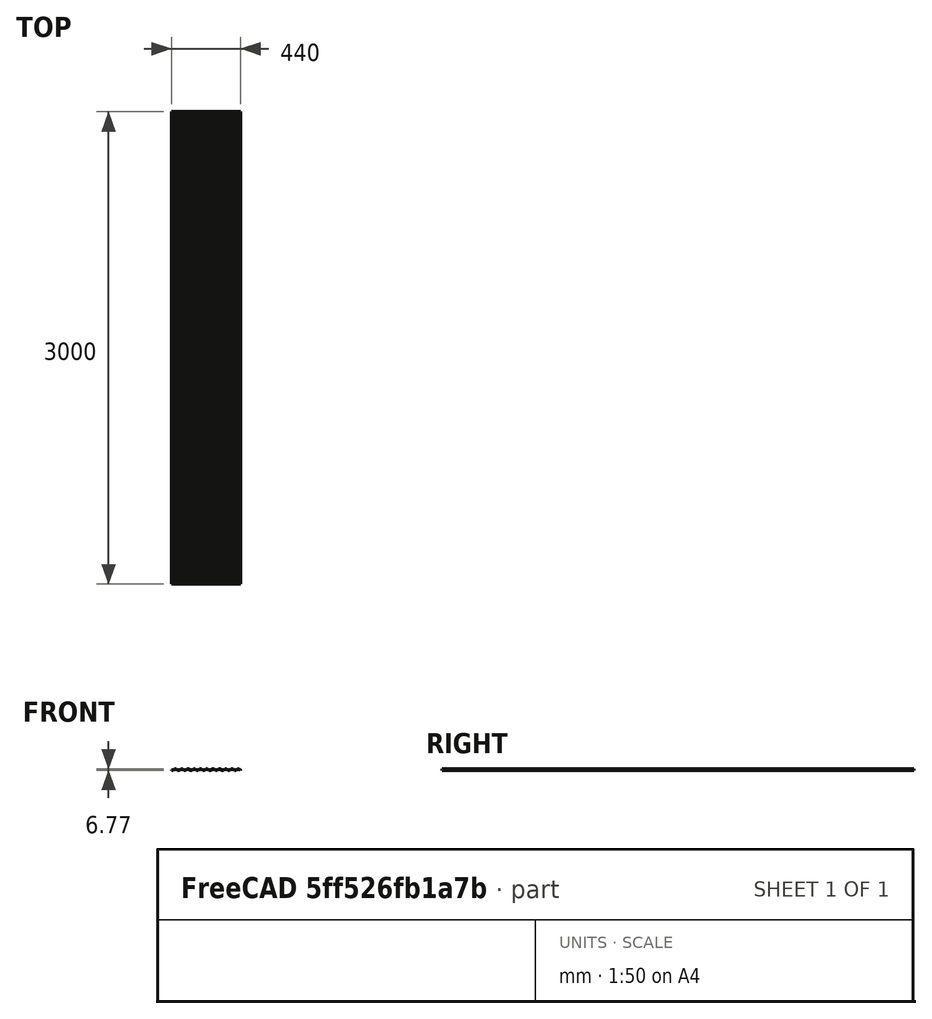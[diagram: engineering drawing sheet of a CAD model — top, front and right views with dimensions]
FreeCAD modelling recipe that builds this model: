
FCSTD DOCUMENT  (FreeCAD 1.0R38641 +468 (Git))
Label: vlnity-plech
License: All rights reserved
LicenseURL: https://en.wikipedia.org/wiki/All_rights_reserved
objects: Sketcher::SketchObject×1, PartDesign::Pad×1, PartDesign::Body×1
note: 6 computed .brp shape members not serialized (recipe doc carries the construction recipe); baked Part::Feature solids carry a one-line shape summary decoded from their .brp

FEATURE [Sketcher::SketchObject] Sketch
  ArcFitTolerance = 1e-06
  AttachmentSupport = -> [XZ_Plane]
  FullyConstrained = true
  MakeInternals = false
  MapMode = 5
  Placement = pos=(0,0,0) rot=(1,0,0;1.5708rad)
  sketch-geometry (90):
    g0: LineSegment StartX=0 StartY=0 StartZ=0 EndX=10 EndY=0 EndZ=0
    g1: LineSegment StartX=10 StartY=0 StartZ=0 EndX=20 EndY=5.7735 EndZ=0
    g2: LineSegment StartX=20 StartY=5.7735 StartZ=0 EndX=30 EndY=5.7735 EndZ=0
    g3: LineSegment StartX=30 StartY=5.7735 StartZ=0 EndX=40 EndY=0 EndZ=0
    g4: LineSegment StartX=0 StartY=1 StartZ=0 EndX=10 EndY=1 EndZ=0
    g5: LineSegment StartX=10 StartY=1 StartZ=0 EndX=20 EndY=6.7735 EndZ=0
    g6: LineSegment StartX=20 StartY=6.7735 StartZ=0 EndX=30 EndY=6.7735 EndZ=0
    g7: LineSegment StartX=30 StartY=6.7735 StartZ=0 EndX=40 EndY=1 EndZ=0
    g8: LineSegment StartX=40 StartY=0 StartZ=0 EndX=50 EndY=0 EndZ=0
    g9: LineSegment StartX=50 StartY=0 StartZ=0 EndX=60 EndY=5.7735 EndZ=0
    g10: LineSegment StartX=60 StartY=5.7735 StartZ=0 EndX=70 EndY=5.7735 EndZ=0
    g11: LineSegment StartX=70 StartY=5.7735 StartZ=0 EndX=80 EndY=0 EndZ=0
    g12: LineSegment StartX=40 StartY=1 StartZ=0 EndX=50 EndY=1 EndZ=0
    g13: LineSegment StartX=50 StartY=1 StartZ=0 EndX=60 EndY=6.7735 EndZ=0
    g14: LineSegment StartX=60 StartY=6.7735 StartZ=0 EndX=70 EndY=6.7735 EndZ=0
    g15: LineSegment StartX=70 StartY=6.7735 StartZ=0 EndX=80 EndY=1 EndZ=0
    g16: LineSegment StartX=80 StartY=0 StartZ=0 EndX=90 EndY=0 EndZ=0
    g17: LineSegment StartX=90 StartY=0 StartZ=0 EndX=100 EndY=5.7735 EndZ=0
    g18: LineSegment StartX=100 StartY=5.7735 StartZ=0 EndX=110 EndY=5.7735 EndZ=0
    g19: LineSegment StartX=110 StartY=5.7735 StartZ=0 EndX=120 EndY=0 EndZ=0
    g20: LineSegment StartX=80 StartY=1 StartZ=0 EndX=90 EndY=1 EndZ=0
    g21: LineSegment StartX=90 StartY=1 StartZ=0 EndX=100 EndY=6.7735 EndZ=0
    g22: LineSegment StartX=100 StartY=6.7735 StartZ=0 EndX=110 EndY=6.7735 EndZ=0
    g23: LineSegment StartX=110 StartY=6.7735 StartZ=0 EndX=120 EndY=1 EndZ=0
    g24: LineSegment StartX=120 StartY=0 StartZ=0 EndX=130 EndY=0 EndZ=0
    g25: LineSegment StartX=130 StartY=0 StartZ=0 EndX=140 EndY=5.7735 EndZ=0
    g26: LineSegment StartX=140 StartY=5.7735 StartZ=0 EndX=150 EndY=5.7735 EndZ=0
    g27: LineSegment StartX=150 StartY=5.7735 StartZ=0 EndX=160 EndY=0 EndZ=0
    g28: LineSegment StartX=120 StartY=1 StartZ=0 EndX=130 EndY=1 EndZ=0
    g29: LineSegment StartX=130 StartY=1 StartZ=0 EndX=140 EndY=6.7735 EndZ=0
    g30: LineSegment StartX=140 StartY=6.7735 StartZ=0 EndX=150 EndY=6.7735 EndZ=0
    g31: LineSegment StartX=150 StartY=6.7735 StartZ=0 EndX=160 EndY=1 EndZ=0
    g32: LineSegment StartX=160 StartY=0 StartZ=0 EndX=170 EndY=0 EndZ=0
    g33: LineSegment StartX=170 StartY=0 StartZ=0 EndX=180 EndY=5.7735 EndZ=0
    g34: LineSegment StartX=180 StartY=5.7735 StartZ=0 EndX=190 EndY=5.7735 EndZ=0
    g35: LineSegment StartX=190 StartY=5.7735 StartZ=0 EndX=200 EndY=0 EndZ=0
    g36: LineSegment StartX=160 StartY=1 StartZ=0 EndX=170 EndY=1 EndZ=0
    g37: LineSegment StartX=170 StartY=1 StartZ=0 EndX=180 EndY=6.7735 EndZ=0
    g38: LineSegment StartX=180 StartY=6.7735 StartZ=0 EndX=190 EndY=6.7735 EndZ=0
    g39: LineSegment StartX=190 StartY=6.7735 StartZ=0 EndX=200 EndY=1 EndZ=0
    g40: LineSegment StartX=200 StartY=0 StartZ=0 EndX=210 EndY=0 EndZ=0
    g41: LineSegment StartX=210 StartY=0 StartZ=0 EndX=220 EndY=5.7735 EndZ=0
    g42: LineSegment StartX=220 StartY=5.7735 StartZ=0 EndX=230 EndY=5.7735 EndZ=0
    g43: LineSegment StartX=230 StartY=5.7735 StartZ=0 EndX=240 EndY=0 EndZ=0
    g44: LineSegment StartX=200 StartY=1 StartZ=0 EndX=210 EndY=1 EndZ=0
    g45: LineSegment StartX=210 StartY=1 StartZ=0 EndX=220 EndY=6.7735 EndZ=0
    g46: LineSegment StartX=220 StartY=6.7735 StartZ=0 EndX=230 EndY=6.7735 EndZ=0
    g47: LineSegment StartX=230 StartY=6.7735 StartZ=0 EndX=240 EndY=1 EndZ=0
    g48: LineSegment StartX=240 StartY=0 StartZ=0 EndX=250 EndY=0 EndZ=0
    g49: LineSegment StartX=250 StartY=0 StartZ=0 EndX=260 EndY=5.7735 EndZ=0
    g50: LineSegment StartX=260 StartY=5.7735 StartZ=0 EndX=270 EndY=5.7735 EndZ=0
    g51: LineSegment StartX=270 StartY=5.7735 StartZ=0 EndX=280 EndY=0 EndZ=0
    g52: LineSegment StartX=240 StartY=1 StartZ=0 EndX=250 EndY=1 EndZ=0
    g53: LineSegment StartX=250 StartY=1 StartZ=0 EndX=260 EndY=6.7735 EndZ=0
    g54: LineSegment StartX=260 StartY=6.7735 StartZ=0 EndX=270 EndY=6.7735 EndZ=0
    g55: LineSegment StartX=270 StartY=6.7735 StartZ=0 EndX=280 EndY=1 EndZ=0
    g56: LineSegment StartX=280 StartY=0 StartZ=0 EndX=290 EndY=0 EndZ=0
    g57: LineSegment StartX=290 StartY=0 StartZ=0 EndX=300 EndY=5.7735 EndZ=0
    g58: LineSegment StartX=300 StartY=5.7735 StartZ=0 EndX=310 EndY=5.7735 EndZ=0
    g59: LineSegment StartX=310 StartY=5.7735 StartZ=0 EndX=320 EndY=0 EndZ=0
    g60: LineSegment StartX=280 StartY=1 StartZ=0 EndX=290 EndY=1 EndZ=0
    g61: LineSegment StartX=290 StartY=1 StartZ=0 EndX=300 EndY=6.7735 EndZ=0
    g62: LineSegment StartX=300 StartY=6.7735 StartZ=0 EndX=310 EndY=6.7735 EndZ=0
    g63: LineSegment StartX=310 StartY=6.7735 StartZ=0 EndX=320 EndY=1 EndZ=0
    g64: LineSegment StartX=320 StartY=0 StartZ=0 EndX=330 EndY=0 EndZ=0
    g65: LineSegment StartX=330 StartY=0 StartZ=0 EndX=340 EndY=5.7735 EndZ=0
    g66: LineSegment StartX=340 StartY=5.7735 StartZ=0 EndX=350 EndY=5.7735 EndZ=0
    g67: LineSegment StartX=350 StartY=5.7735 StartZ=0 EndX=360 EndY=0 EndZ=0
    g68: LineSegment StartX=320 StartY=1 StartZ=0 EndX=330 EndY=1 EndZ=0
    g69: LineSegment StartX=330 StartY=1 StartZ=0 EndX=340 EndY=6.7735 EndZ=0
    g70: LineSegment StartX=340 StartY=6.7735 StartZ=0 EndX=350 EndY=6.7735 EndZ=0
    g71: LineSegment StartX=350 StartY=6.7735 StartZ=0 EndX=360 EndY=1 EndZ=0
    g72: LineSegment StartX=360 StartY=0 StartZ=0 EndX=370 EndY=0 EndZ=0
    g73: LineSegment StartX=370 StartY=0 StartZ=0 EndX=380 EndY=5.7735 EndZ=0
    g74: LineSegment StartX=380 StartY=5.7735 StartZ=0 EndX=390 EndY=5.7735 EndZ=0
    g75: LineSegment StartX=390 StartY=5.7735 StartZ=0 EndX=400 EndY=0 EndZ=0
    g76: LineSegment StartX=360 StartY=1 StartZ=0 EndX=370 EndY=1 EndZ=0
    g77: LineSegment StartX=370 StartY=1 StartZ=0 EndX=380 EndY=6.7735 EndZ=0
    g78: LineSegment StartX=380 StartY=6.7735 StartZ=0 EndX=390 EndY=6.7735 EndZ=0
    g79: LineSegment StartX=390 StartY=6.7735 StartZ=0 EndX=400 EndY=1 EndZ=0
    g80: LineSegment StartX=400 StartY=0 StartZ=0 EndX=410 EndY=0 EndZ=0
    g81: LineSegment StartX=410 StartY=0 StartZ=0 EndX=420 EndY=5.7735 EndZ=0
    g82: LineSegment StartX=420 StartY=5.7735 StartZ=0 EndX=430 EndY=5.7735 EndZ=0
    g83: LineSegment StartX=430 StartY=5.7735 StartZ=0 EndX=440 EndY=0 EndZ=0
    g84: LineSegment StartX=400 StartY=1 StartZ=0 EndX=410 EndY=1 EndZ=0
    g85: LineSegment StartX=410 StartY=1 StartZ=0 EndX=420 EndY=6.7735 EndZ=0
    g86: LineSegment StartX=420 StartY=6.7735 StartZ=0 EndX=430 EndY=6.7735 EndZ=0
    g87: LineSegment StartX=430 StartY=6.7735 StartZ=0 EndX=440 EndY=1 EndZ=0
    g88: LineSegment StartX=0 StartY=1 StartZ=0 EndX=0 EndY=0 EndZ=0
    g89: LineSegment StartX=440 StartY=1 StartZ=0 EndX=440 EndY=0 EndZ=0
  constraints (279):
    c: Coincident(g0,g-1)
    c: PointOnObject(g0,g-1)
    c: Coincident(g1,g0)
    c: Coincident(g2,g1)
    c: Horizontal(g2)
    c: Coincident(g3,g2)
    c: PointOnObject(g3,g-1)
    c: Equal(g0,g2)
    c: Equal(g1,g3)
    c: Angle(g-1,g1) = 0.523599
    c: DistanceX(g0,g0) = 10
    c: DistanceX(g0,g1) = 10
    c: Coincident(g5,g4)
    c: Coincident(g6,g5)
    c: Horizontal(g6)
    c: Coincident(g7,g6)
    c: Equal(g4,g6)
    c: Equal(g5,g7)
    c: DistanceX(g4,g4) = 10
    c: DistanceX(g4,g5) = 10
    c: DistanceY(g0,g4) = 1
    c: Parallel(g4,g0)
    c: Vertical(g4,g0)
    c: Parallel(g5,g1)
    c: Parallel(g7,g3)
    c: Coincident(g9,g8)
    c: Coincident(g17,g16)
    c: Coincident(g25,g24)
    c: Coincident(g33,g32)
    c: Coincident(g41,g40)
    c: Coincident(g49,g48)
    c: Coincident(g57,g56)
    c: Coincident(g65,g64)
    c: Coincident(g73,g72)
    c: Coincident(g81,g80)
    c: Coincident(g10,g9)
    c: Coincident(g18,g17)
    c: Coincident(g26,g25)
    c: Coincident(g34,g33)
    c: Coincident(g42,g41)
    c: Coincident(g50,g49)
    c: Coincident(g58,g57)
    c: Coincident(g66,g65)
    c: Coincident(g74,g73)
    c: Coincident(g82,g81)
    c: Horizontal(g10)
    c: Horizontal(g18)
    c: Horizontal(g26)
    c: Horizontal(g34)
    c: Horizontal(g42)
    c: Horizontal(g50)
    c: Horizontal(g58)
    c: Horizontal(g66)
    c: Horizontal(g74)
    c: Horizontal(g82)
    c: Coincident(g11,g10)
    c: Coincident(g19,g18)
    c: Coincident(g27,g26)
    c: Coincident(g35,g34)
    c: Coincident(g43,g42)
    c: Coincident(g51,g50)
    c: Coincident(g59,g58)
    c: Coincident(g67,g66)
    c: Coincident(g75,g74)
    c: Coincident(g83,g82)
    c: Equal(g8,g10)
    c: Equal(g16,g18)
    c: Equal(g24,g26)
    c: Equal(g32,g34)
    c: Equal(g40,g42)
    c: Equal(g48,g50)
    c: Equal(g56,g58)
    c: Equal(g64,g66)
    c: Equal(g72,g74)
    c: Equal(g80,g82)
    c: Equal(g9,g11)
    c: Equal(g17,g19)
    c: Equal(g25,g27)
    c: Equal(g33,g35)
    c: Equal(g41,g43)
    c: Equal(g49,g51)
    c: Equal(g57,g59)
    c: Equal(g65,g67)
    c: Equal(g73,g75)
    c: Equal(g81,g83)
    c: DistanceX(g8,g8) = 10
    c: DistanceX(g16,g16) = 10
    c: DistanceX(g24,g24) = 10
    c: DistanceX(g32,g32) = 10
    c: DistanceX(g40,g40) = 10
    c: DistanceX(g48,g48) = 10
    c: DistanceX(g56,g56) = 10
    c: DistanceX(g64,g64) = 10
    c: DistanceX(g72,g72) = 10
    c: DistanceX(g80,g80) = 10
    c: DistanceX(g8,g9) = 10
    c: DistanceX(g16,g17) = 10
    c: DistanceX(g24,g25) = 10
    c: DistanceX(g32,g33) = 10
    c: DistanceX(g40,g41) = 10
    c: DistanceX(g48,g49) = 10
    c: DistanceX(g56,g57) = 10
    c: DistanceX(g64,g65) = 10
    c: DistanceX(g72,g73) = 10
    c: DistanceX(g80,g81) = 10
    c: Coincident(g13,g12)
    c: Coincident(g21,g20)
    c: Coincident(g29,g28)
    c: Coincident(g37,g36)
    c: Coincident(g45,g44)
    c: Coincident(g53,g52)
    c: Coincident(g61,g60)
    c: Coincident(g69,g68)
    c: Coincident(g77,g76)
    c: Coincident(g85,g84)
    c: Coincident(g14,g13)
    c: Coincident(g22,g21)
    c: Coincident(g30,g29)
    c: Coincident(g38,g37)
    c: Coincident(g46,g45)
    c: Coincident(g54,g53)
    c: Coincident(g62,g61)
    c: Coincident(g70,g69)
    c: Coincident(g78,g77)
    c: Coincident(g86,g85)
    c: Horizontal(g14)
    c: Horizontal(g22)
    c: Horizontal(g30)
    c: Horizontal(g38)
    c: Horizontal(g46)
    c: Horizontal(g54)
    c: Horizontal(g62)
    c: Horizontal(g70)
    c: Horizontal(g78)
    c: Horizontal(g86)
    c: Coincident(g15,g14)
    c: Coincident(g23,g22)
    c: Coincident(g31,g30)
    c: Coincident(g39,g38)
    c: Coincident(g47,g46)
    c: Coincident(g55,g54)
    c: Coincident(g63,g62)
    c: Coincident(g71,g70)
    c: Coincident(g79,g78)
    c: Coincident(g87,g86)
    c: Equal(g12,g14)
    c: Equal(g20,g22)
    c: Equal(g28,g30)
    c: Equal(g36,g38)
    c: Equal(g44,g46)
    c: Equal(g52,g54)
    c: Equal(g60,g62)
    c: Equal(g68,g70)
    c: Equal(g76,g78)
    c: Equal(g84,g86)
    c: Equal(g13,g15)
    c: Equal(g21,g23)
    c: Equal(g29,g31)
    c: Equal(g37,g39)
    c: Equal(g45,g47)
    c: Equal(g53,g55)
    c: Equal(g61,g63)
    c: Equal(g69,g71)
    c: Equal(g77,g79)
    c: Equal(g85,g87)
    c: DistanceX(g12,g12) = 10
    c: DistanceX(g20,g20) = 10
    c: DistanceX(g28,g28) = 10
    c: DistanceX(g36,g36) = 10
    c: DistanceX(g44,g44) = 10
    c: DistanceX(g52,g52) = 10
    c: DistanceX(g60,g60) = 10
    c: DistanceX(g68,g68) = 10
    c: DistanceX(g76,g76) = 10
    c: DistanceX(g84,g84) = 10
    c: DistanceX(g12,g13) = 10
    c: DistanceX(g20,g21) = 10
    c: DistanceX(g28,g29) = 10
    c: DistanceX(g36,g37) = 10
    c: DistanceX(g44,g45) = 10
    c: DistanceX(g52,g53) = 10
    c: DistanceX(g60,g61) = 10
    c: DistanceX(g68,g69) = 10
    c: DistanceX(g76,g77) = 10
    c: DistanceX(g84,g85) = 10
    c: DistanceY(g8,g12) = 1
    c: DistanceY(g16,g20) = 1
    c: DistanceY(g24,g28) = 1
    c: DistanceY(g32,g36) = 1
    c: DistanceY(g40,g44) = 1
    c: DistanceY(g48,g52) = 1
    c: DistanceY(g56,g60) = 1
    c: DistanceY(g64,g68) = 1
    c: DistanceY(g72,g76) = 1
    c: DistanceY(g80,g84) = 1
    c: Parallel(g12,g8)
    c: Parallel(g20,g16)
    c: Parallel(g28,g24)
    c: Parallel(g36,g32)
    c: Parallel(g44,g40)
    c: Parallel(g52,g48)
    c: Parallel(g60,g56)
    c: Parallel(g68,g64)
    c: Parallel(g76,g72)
    c: Parallel(g84,g80)
    c: Vertical(g12,g8)
    c: Vertical(g20,g16)
    c: Vertical(g28,g24)
    c: Vertical(g36,g32)
    c: Vertical(g44,g40)
    c: Vertical(g52,g48)
    c: Vertical(g60,g56)
    c: Vertical(g68,g64)
    c: Vertical(g76,g72)
    c: Vertical(g84,g80)
    c: Parallel(g13,g9)
    c: Parallel(g21,g17)
    c: Parallel(g29,g25)
    c: Parallel(g37,g33)
    c: Parallel(g45,g41)
    c: Parallel(g53,g49)
    c: Parallel(g61,g57)
    c: Parallel(g69,g65)
    c: Parallel(g77,g73)
    c: Parallel(g85,g81)
    c: Parallel(g15,g11)
    c: Parallel(g23,g19)
    c: Parallel(g31,g27)
    c: Parallel(g39,g35)
    c: Parallel(g47,g43)
    c: Parallel(g55,g51)
    c: Parallel(g63,g59)
    c: Parallel(g71,g67)
    c: Parallel(g79,g75)
    c: Parallel(g87,g83)
    c: Coincident(g12,g7)
    c: PointOnObject(g8,g-1)
    c: Coincident(g11,g16)
    c: PointOnObject(g11,g-1)
    c: PointOnObject(g16,g-1)
    c: Coincident(g19,g24)
    c: PointOnObject(g24,g-1)
    c: PointOnObject(g19,g-1)
    c: Coincident(g27,g32)
    c: PointOnObject(g27,g-1)
    c: PointOnObject(g40,g-1)
    c: Coincident(g35,g40)
    c: Coincident(g43,g48)
    c: PointOnObject(g43,g-1)
    c: Coincident(g51,g56)
    c: Coincident(g59,g64)
    c: Coincident(g67,g72)
    c: Coincident(g75,g80)
    c: PointOnObject(g56,g-1)
    c: PointOnObject(g64,g-1)
    c: PointOnObject(g59,g-1)
    c: PointOnObject(g67,g-1)
    c: PointOnObject(g72,g-1)
    c: PointOnObject(g75,g-1)
    c: PointOnObject(g80,g-1)
    c: PointOnObject(g48,g-1)
    c: PointOnObject(g51,g-1)
    c: Parallel(g9,g1)
    c: Parallel(g17,g9)
    c: Parallel(g27,g19)
    c: PointOnObject(g32,g-1)
    c: Parallel(g33,g25)
    c: PointOnObject(g40,g-1)
    c: Parallel(g41,g33)
    c: Parallel(g49,g41)
    c: Parallel(g57,g49)
    c: Parallel(g65,g57)
    c: Parallel(g73,g65)
    c: Parallel(g81,g73)
    c: PointOnObject(g83,g-1)
    c: Coincident(g88,g4)
    c: Coincident(g88,g0)
    c: Coincident(g89,g87)
    c: Coincident(g89,g83)
FEATURE [PartDesign::Pad] Pad
  Direction = (0,-1,2e-16)
  Length = 3000
  Length2 = 10
  Placement = pos=(0,0,0) rot=(1,0,0;1.5708rad)
  Profile = -> Sketch
  ReferenceAxis = -> Sketch [N_Axis]
  Refine = true
  Suppressed = false
  Type = 0
FEATURE [PartDesign::Body] Body  label="strecha-trapez"
  AllowCompound = false
  Group = -> [Sketch,Pad]
  Origin = -> Origin
  Tip = -> Pad
